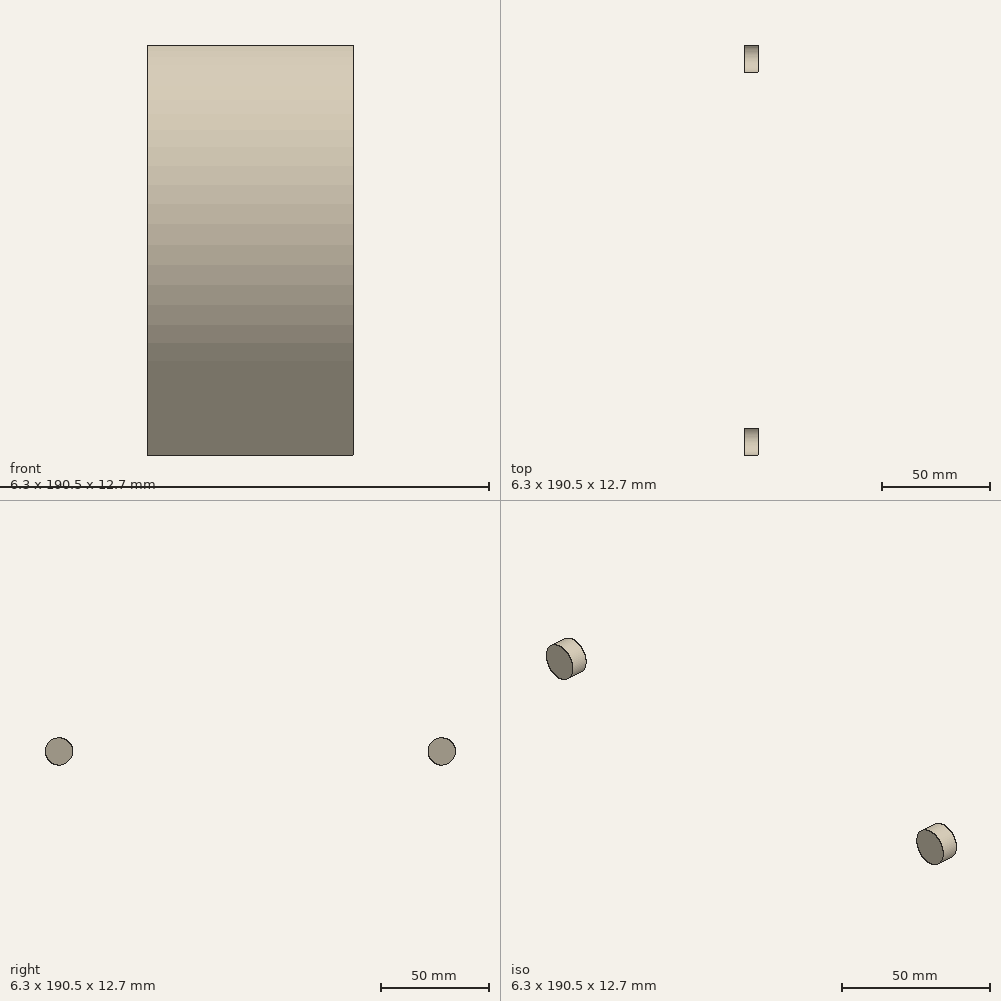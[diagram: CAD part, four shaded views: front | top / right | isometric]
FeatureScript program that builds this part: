
annotation { "Feature Type Name" : "Feature", "Feature Type Description" : "" }
export const myFeature = defineFeature(function(context is Context, id is Id, definition is map)
    precondition{}
    {
        {
            var Q0;
            Q0=qCreatedBy(makeId("Right.planeOp"),FACE);
            var sketch = newSketch(context, id + "F0", { "sketchPlane" : qUnion([Q0])});
            skLineSegment(sketch, "E0.bottom", {"start": v(-108.95, 116.55) * mm, "end": v(119.65, 116.55) * mm});
            skLineSegment(sketch, "E0.top", {"start": v(-108.95, -61.25) * mm, "end": v(119.65, -61.25) * mm});
            skArc(sketch, "E1", {"start": v(-108.95, 116.55) * mm, "mid": v(-161.37, 27.65) * mm, "end": v(-108.95, -61.25) * mm});
            skArc(sketch, "E2", {"start": v(119.65, -61.25) * mm, "mid": v(172.06, 27.65) * mm, "end": v(119.65, 116.55) * mm});
            skSolve(sketch);
        }
        {
            var Q0;
            Q0=makeQuery(id+"F0.imprint","IMPRINT",FACE,{"disambiguationData":[TD([[makeQuery(id+"F0.imprint","IMPRINT",EDGE,{"derivedFrom":sQuery(id+"F0.wireOp",EDGE,"E0.bottom")}),-1.0]])]});
            extrude(context, id + "F1", {"entities" : qUnion([Q0]), "depth" : 6.35 * mm, "offsetDistance" : 25 * mm});
        }
        {
            var Q0;
            Q0=makeQuery(id+"F1.opExtrude","CAP_FACE",FACE,{"disambiguationData":[OSD([sQuery(id+"F0.wireOp",EDGE,"E0.bottom"),sQuery(id+"F0.wireOp",EDGE,"E0.top"),sQuery(id+"F0.wireOp",EDGE,"E1"),sQuery(id+"F0.wireOp",EDGE,"E2")])],"isStart":false});
            var sketch = newSketch(context, id + "F2", { "sketchPlane" : qUnion([Q0])});
            skLineSegment(sketch, "E3", {"start": v(-161.37, 27.65) * mm, "end": v(172.06, 27.65) * mm});
            skPoint(sketch, "E4", {"position": v(-129.62, 27.65) * mm});
            skPoint(sketch, "E5", {"position": v(-40.72, 27.65) * mm});
            skPoint(sketch, "E6", {"position": v(48.18, 27.65) * mm});
            skArc(sketch, "E7", {"start": v(94.25, -61.25) * mm, "mid": v(146.66, 27.65) * mm, "end": v(94.25, 116.55) * mm});
            skSolve(sketch);
        }
        {
            var Q0;
            {var subQ0=sQuery(id+"F2.wireOp",EDGE,"E3");var subQ1=makeQuery(id+"F1.opExtrude","CAP_EDGE",EDGE,{"disambiguationData":[OSD([sQuery(id+"F0.wireOp",EDGE,"E2")])],"isStart":false});var subQ2=makeQuery(id+"F2.imprint","INTERSECT",VERTEX,{"derivedFrom":[subQ1,subQ0]});Q0=makeQuery(id+"F2.imprint","IMPRINT",FACE,{"disambiguationData":[TD([[makeQuery(id+"F2.imprint","IMPRINT",EDGE,{"disambiguationData":[TD([[subQ2,1.0]])],"derivedFrom":subQ0}),1.0]])]});}
            var Q1;
            {var subQ0=sQuery(id+"F2.wireOp",EDGE,"E3");var subQ1=makeQuery(id+"F1.opExtrude","CAP_EDGE",EDGE,{"disambiguationData":[OSD([sQuery(id+"F0.wireOp",EDGE,"E2")])],"isStart":false});var subQ2=makeQuery(id+"F2.imprint","INTERSECT",VERTEX,{"derivedFrom":[subQ1,subQ0]});Q1=makeQuery(id+"F2.imprint","IMPRINT",FACE,{"disambiguationData":[TD([[makeQuery(id+"F2.imprint","IMPRINT",EDGE,{"disambiguationData":[TD([[subQ2,1.0]])],"derivedFrom":subQ0}),-1.0]])]});}
            extrude(context, id + "F3", {"entities" : qUnion([Q0, Q1]), "operationType" : NewBodyOperationType.REMOVE, "oppositeDirection" : true, "depth" : 25 * mm, "offsetDistance" : 25 * mm});
        }
        {
            var Q0;
            Q0=makeQuery(id+"F1.opExtrude","CAP_FACE",FACE,{"disambiguationData":[OSD([sQuery(id+"F0.wireOp",EDGE,"E0.bottom"),sQuery(id+"F0.wireOp",EDGE,"E0.top"),sQuery(id+"F0.wireOp",EDGE,"E1"),sQuery(id+"F0.wireOp",EDGE,"E2")])],"isStart":false});
            var sketch = newSketch(context, id + "F4", { "sketchPlane" : qUnion([Q0])});
            skLineSegment(sketch, "E8", {"start": v(-161.37, 27.65) * mm, "end": v(146.66, 27.65) * mm});
            skPoint(sketch, "E9", {"position": v(-129.62, 27.65) * mm});
            skPoint(sketch, "E10", {"position": v(-40.72, 27.65) * mm});
            skPoint(sketch, "E11", {"position": v(48.18, 27.65) * mm});
            skCircle(sketch, "E12", {"center": v(-129.62, 27.65) * mm, "radius": 6.35 * mm});
            skCircle(sketch, "E13", {"center": v(-40.72, 27.65) * mm, "radius": 6.35 * mm});
            skCircle(sketch, "E14", {"center": v(48.18, 27.65) * mm, "radius": 6.35 * mm});
            skSolve(sketch);
        }
        {
            var Q0;
            {var subQ0=sQuery(id+"F4.wireOp",EDGE,"E12");var subQ1=sQuery(id+"F4.wireOp",EDGE,"E8");var subQ2=makeQuery(id+"F4.imprint","INTERSECT",VERTEX,{"disambiguationData":[OD(0.0)],"derivedFrom":[subQ1,subQ0]});Q0=makeQuery(id+"F4.imprint","IMPRINT",FACE,{"disambiguationData":[TD([[makeQuery(id+"F4.imprint","IMPRINT",EDGE,{"disambiguationData":[TD([[subQ2,-1.0]])],"derivedFrom":subQ1}),-1.0]])]});}
            var Q1;
            {var subQ0=sQuery(id+"F4.wireOp",EDGE,"E13");var subQ1=sQuery(id+"F4.wireOp",EDGE,"E8");var subQ2=makeQuery(id+"F4.imprint","INTERSECT",VERTEX,{"disambiguationData":[OD(0.0)],"derivedFrom":[subQ1,subQ0]});Q1=makeQuery(id+"F4.imprint","IMPRINT",FACE,{"disambiguationData":[TD([[makeQuery(id+"F4.imprint","IMPRINT",EDGE,{"disambiguationData":[TD([[subQ2,-1.0]])],"derivedFrom":subQ1}),1.0]])]});}
            var Q2;
            {var subQ0=sQuery(id+"F4.wireOp",EDGE,"E13");var subQ1=sQuery(id+"F4.wireOp",EDGE,"E8");var subQ2=makeQuery(id+"F4.imprint","INTERSECT",VERTEX,{"disambiguationData":[OD(0.0)],"derivedFrom":[subQ1,subQ0]});Q2=makeQuery(id+"F4.imprint","IMPRINT",FACE,{"disambiguationData":[TD([[makeQuery(id+"F4.imprint","IMPRINT",EDGE,{"disambiguationData":[TD([[subQ2,-1.0]])],"derivedFrom":subQ1}),-1.0]])]});}
            var Q3;
            {var subQ0=sQuery(id+"F4.wireOp",EDGE,"E14");var subQ1=sQuery(id+"F4.wireOp",EDGE,"E8");var subQ2=makeQuery(id+"F4.imprint","INTERSECT",VERTEX,{"disambiguationData":[OD(0.0)],"derivedFrom":[subQ1,subQ0]});Q3=makeQuery(id+"F4.imprint","IMPRINT",FACE,{"disambiguationData":[TD([[makeQuery(id+"F4.imprint","IMPRINT",EDGE,{"disambiguationData":[TD([[subQ2,-1.0]])],"derivedFrom":subQ1}),1.0]])]});}
            var Q4;
            {var subQ0=sQuery(id+"F4.wireOp",EDGE,"E14");var subQ1=sQuery(id+"F4.wireOp",EDGE,"E8");var subQ2=makeQuery(id+"F4.imprint","INTERSECT",VERTEX,{"disambiguationData":[OD(0.0)],"derivedFrom":[subQ1,subQ0]});Q4=makeQuery(id+"F4.imprint","IMPRINT",FACE,{"disambiguationData":[TD([[makeQuery(id+"F4.imprint","IMPRINT",EDGE,{"disambiguationData":[TD([[subQ2,-1.0]])],"derivedFrom":subQ1}),-1.0]])]});}
            var Q5;
            {var subQ0=sQuery(id+"F4.wireOp",EDGE,"E12");var subQ1=sQuery(id+"F4.wireOp",EDGE,"E8");var subQ2=makeQuery(id+"F4.imprint","INTERSECT",VERTEX,{"disambiguationData":[OD(0.0)],"derivedFrom":[subQ1,subQ0]});Q5=makeQuery(id+"F4.imprint","IMPRINT",FACE,{"disambiguationData":[TD([[makeQuery(id+"F4.imprint","IMPRINT",EDGE,{"disambiguationData":[TD([[subQ2,-1.0]])],"derivedFrom":subQ1}),1.0]])]});}
            extrude(context, id + "F5", {"entities" : qUnion([Q0, Q1, Q2, Q3, Q4, Q5]), "operationType" : NewBodyOperationType.REMOVE, "oppositeDirection" : true, "depth" : 25 * mm, "offsetDistance" : 25 * mm});
        }
    });
